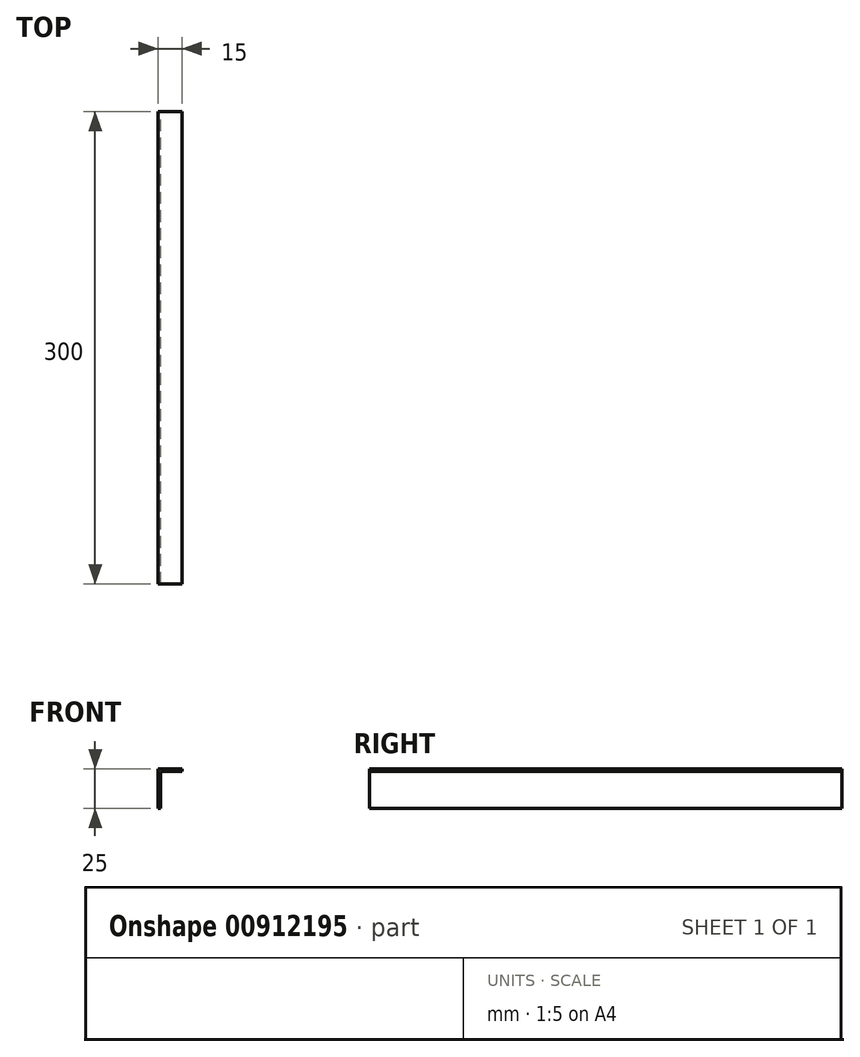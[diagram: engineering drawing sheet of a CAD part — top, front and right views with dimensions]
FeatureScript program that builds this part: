
annotation { "Feature Type Name" : "Feature", "Feature Type Description" : "" }
export const myFeature = defineFeature(function(context is Context, id is Id, definition is map)
    precondition{}
    {
        {
            var Q0;
            Q0=qCreatedBy(makeId("Front.planeOp"),FACE);
            var sketch = newSketch(context, id + "F0", { "sketchPlane" : qUnion([Q0])});
            skLineSegment(sketch, "E0", {"start": v(0, 0) * mm, "end": v(0, 25) * mm});
            skLineSegment(sketch, "E1", {"start": v(0, 25) * mm, "end": v(15, 25) * mm});
            skLineSegment(sketch, "E2", {"start": v(15, 25) * mm, "end": v(15, 23.41) * mm});
            skLineSegment(sketch, "E3", {"start": v(15, 23.41) * mm, "end": v(1.59, 23.41) * mm});
            skLineSegment(sketch, "E4", {"start": v(1.59, 23.41) * mm, "end": v(1.59, 0) * mm});
            skLineSegment(sketch, "E5", {"start": v(1.59, 0) * mm, "end": v(0, 0) * mm});
            skSolve(sketch);
        }
        {
            var Q0;
            Q0 = qSketchRegion(id + "F0", true);
            extrude(context, id + "F1", {"entities" : qUnion([Q0]), "depth" : 300 * mm, "offsetDistance" : 25 * mm});
        }
    });
